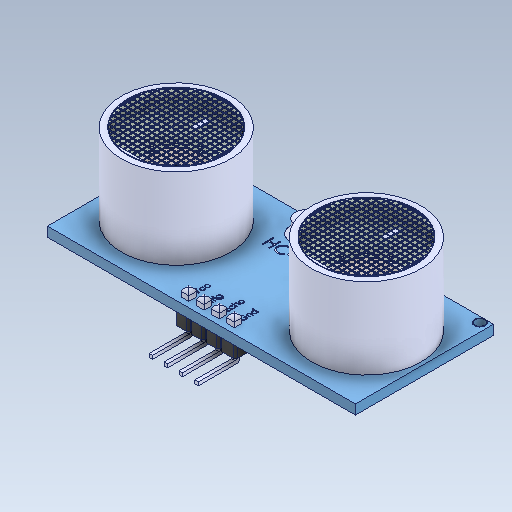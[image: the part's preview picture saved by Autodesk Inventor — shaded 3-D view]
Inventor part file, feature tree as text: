
AUTODESK INVENTOR PART (.ipt)
format: ipt  version: 2021 (Build 250183000, 183)  size: 2,562,048 bytes
history: mixed  units: mm
features: other x17, chamfer x1, imported_body x1
ambient origin geometry x8: Origin, YZ Plane, XZ Plane, XY Plane, X Axis, Y Axis, Z Axis, Center Point
bodies: Body1 (imported_parasolid), Body2 (imported_parasolid), Body3 (imported_parasolid), Body4 (imported_parasolid), Body5 (imported_parasolid), Body6 (imported_parasolid), Body7 (imported_parasolid), Body8 (imported_parasolid), Body9 (imported_parasolid)
feature tree (19):
  other  "Sólido1"
  other  "Sólido2"
  other  "Sólido3"
  other  "Sólido4"
  other  "Sólido5"
  other  "Sólido6"
  other  "Sólido7"
  other  "Sólido8"
  other  "Sólido9"
  other  "Cortar-Extruir15[1]"
  other  "Cortar-Extruir15[1]:1"
  other  "Cortar-Extruir15[1]:2"
  other  "Cortar-Extruir15[1]:3"
  other  "Cortar-Extruir15[2]"
  other  "Cortar-Extruir15[2]:1"
  other  "Cortar-Extruir15[2]:2"
  other  "Cortar-Extruir15[2]:3"
  chamfer  "Chaflán3"  [1 undecoded]
  imported_body  NMx_Import_Brep_tag  [imported B-rep: ~254 faces, bbox_mm=[44.6, 16.7, 24.194595]]
note: 1 required parameter value undecoded (feature->parameter linkage not recoverable at this tier; creation-order binding heuristic only, values carry confidence <= 0.55)
